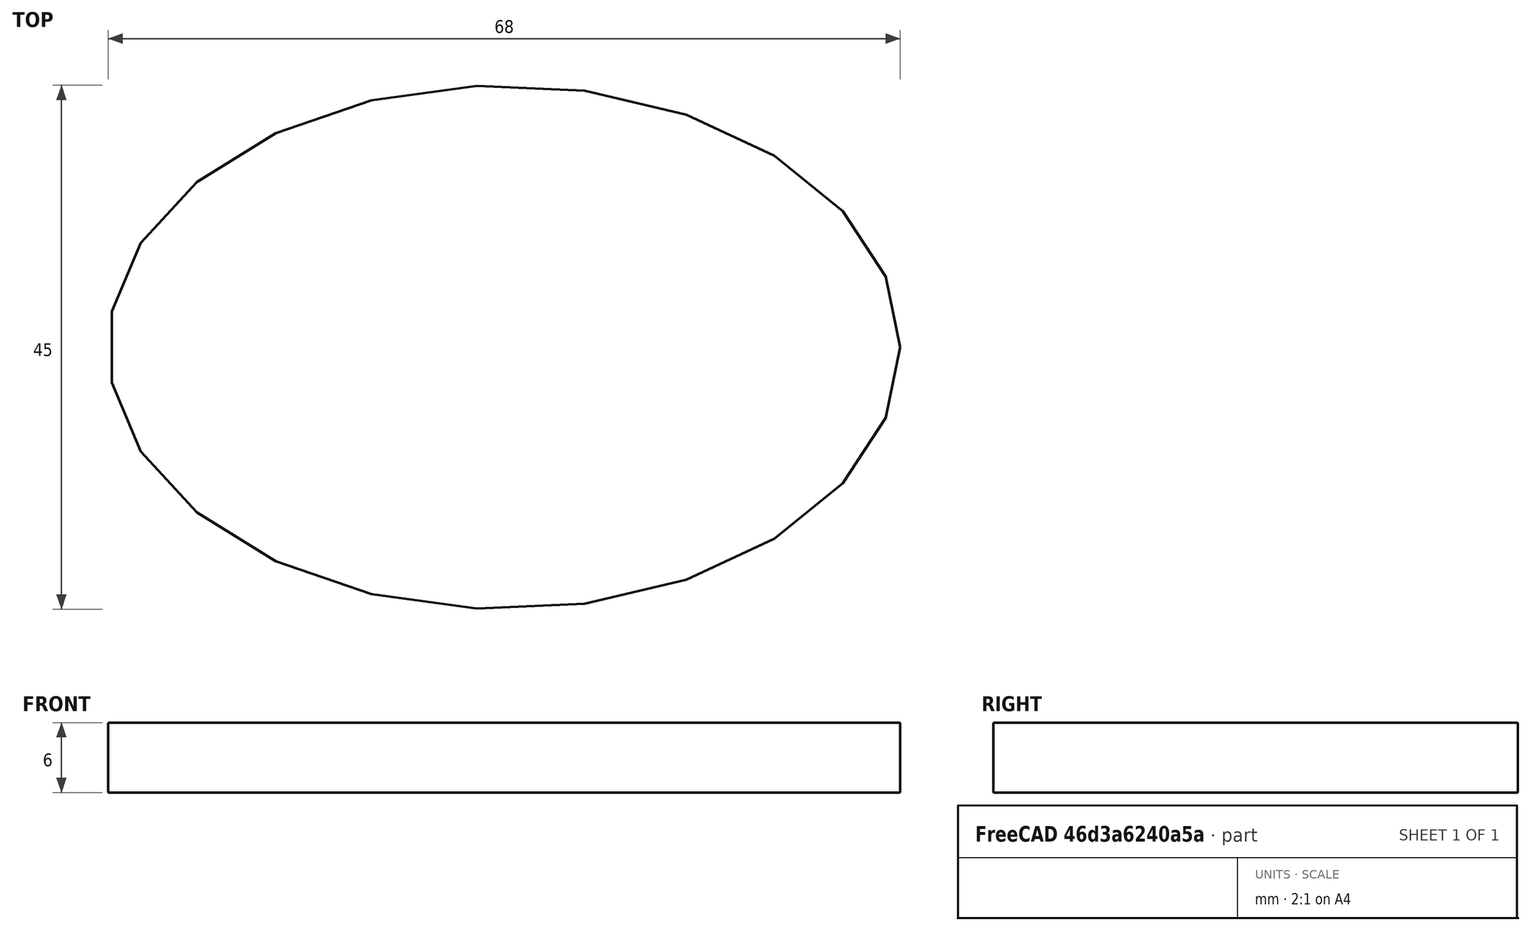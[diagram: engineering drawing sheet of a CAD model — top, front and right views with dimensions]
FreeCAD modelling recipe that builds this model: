
FCSTD DOCUMENT  (FreeCAD 0.17R13541 (Git))
Label: Digi-Night-Light-8Dense-LEDS-Oval-USB-V0.10
License: All rights reserved
LicenseURL: http://en.wikipedia.org/wiki/All_rights_reserved
objects: Sketcher::SketchObject×2, PartDesign::Pad×1, PartDesign::Body×1, App::Part×1
note: 5 computed .brp shape members not serialized (recipe doc carries the construction recipe); baked Part::Feature solids carry a one-line shape summary decoded from their .brp

FEATURE [Sketcher::SketchObject] Sketch
  MapMode = 5
  Support = -> [XY_Plane001]
  sketch-geometry (6):
    g0: Ellipse CenterX=0 CenterY=0 CenterZ=0 NormalX=0 NormalY=0 NormalZ=1 MajorRadius=34 MinorRadius=22.5 AngleXU=0
    g1: LineSegment [constr] StartX=34 StartY=0 StartZ=0 EndX=-34 EndY=0 EndZ=0
    g2: LineSegment [constr] StartX=0 StartY=22.5 StartZ=0 EndX=0 EndY=-22.5 EndZ=0
    g3: GeomPoint X=25.4902 Y=0 Z=0
    g4: GeomPoint X=-25.4902 Y=0 Z=0
    g5: LineSegment StartX=-6.25 StartY=-22.1166 StartZ=0 EndX=6.25 EndY=-22.1166 EndZ=0
  constraints (9):
    c: InternalAlignment(g1-g4 -> g0) x4
    c: Coincident(g0,g-1)
    c: PointOnObject(g2,g-2)
    c: Distance(g2,g2) = 45
    c: Distance(g1,g1) = 68
    c: PointOnObject(g5,g0)
    c: PointOnObject(g5,g0)
    c: Horizontal(g5)
    c: Distance(g5,g5) = 12.5
FEATURE [PartDesign::Pad] Pad
  Length = 6
  Length2 = 100
  Profile = -> Sketch
  Type = 0
FEATURE [Sketcher::SketchObject] Sketch001
  MapMode = 5
  Placement = pos=(0,0,0) rot=(1,0,0;3.14159rad)
  Support = -> [Pad]
  sketch-geometry (10):
    g0: LineSegment StartX=-9.875 StartY=-3.01066 StartZ=0 EndX=9.875 EndY=-3.01066 EndZ=0
    g1: LineSegment StartX=9.875 StartY=-3.01066 StartZ=0 EndX=9.875 EndY=-21.2107 EndZ=0
    g2: LineSegment StartX=9.875 StartY=-21.2107 StartZ=0 EndX=-9.875 EndY=-21.2107 EndZ=0
    g3: LineSegment StartX=-9.875 StartY=-21.2107 StartZ=0 EndX=-9.875 EndY=-3.01066 EndZ=0
    g4: GeomPoint X=0 Y=-21.2107 Z=0
    g5: LineSegment StartX=-27.7096 StartY=8.90897 StartZ=0 EndX=27.7096 EndY=8.90897 EndZ=0
    g6: LineSegment StartX=27.7096 StartY=8.90897 StartZ=0 EndX=27.7096 EndY=-3.09103 EndZ=0
    g7: LineSegment StartX=27.7096 StartY=-3.09103 StartZ=0 EndX=-27.7096 EndY=-3.09103 EndZ=0
    g8: LineSegment StartX=-27.7096 StartY=-3.09103 StartZ=0 EndX=-27.7096 EndY=8.90897 EndZ=0
    g9: GeomPoint X=0 Y=8.90897 Z=0
  constraints (25):
    c: Coincident(g0,g1)
    c: Coincident(g1,g2)
    c: Coincident(g2,g3)
    c: Coincident(g3,g0)
    c: Horizontal(g0)
    c: Horizontal(g2)
    c: Vertical(g1)
    c: Vertical(g3)
    c: Distance(g0) = 19.75
    c: PointOnObject(g4,g2)
    c: Symmetric(g1,g2,g4)
    c: PointOnObject(g4,g-2)
    c: Distance(g1) = 18.2
    c: Coincident(g5,g6)
    c: Coincident(g6,g7)
    c: Coincident(g7,g8)
    c: Coincident(g8,g5)
    c: Horizontal(g5)
    c: Horizontal(g7)
    c: Vertical(g6)
    c: Vertical(g8)
    c: Distance(g8) = 12
    c: PointOnObject(g9,g5)
    c: Symmetric(g5,g5,g9)
    c: PointOnObject(g9,g-2)
FEATURE [PartDesign::Body] Body
  Group = -> [Sketch,Pad,Sketch001]
  Origin = -> Origin001
  Tip = -> Pad
FEATURE [App::Part] Part
  Group = -> [Body]
  License = CC BY 3.0
  LicenseURL = http://creativecommons.org/licenses/by/3.0/
  Origin = -> Origin
